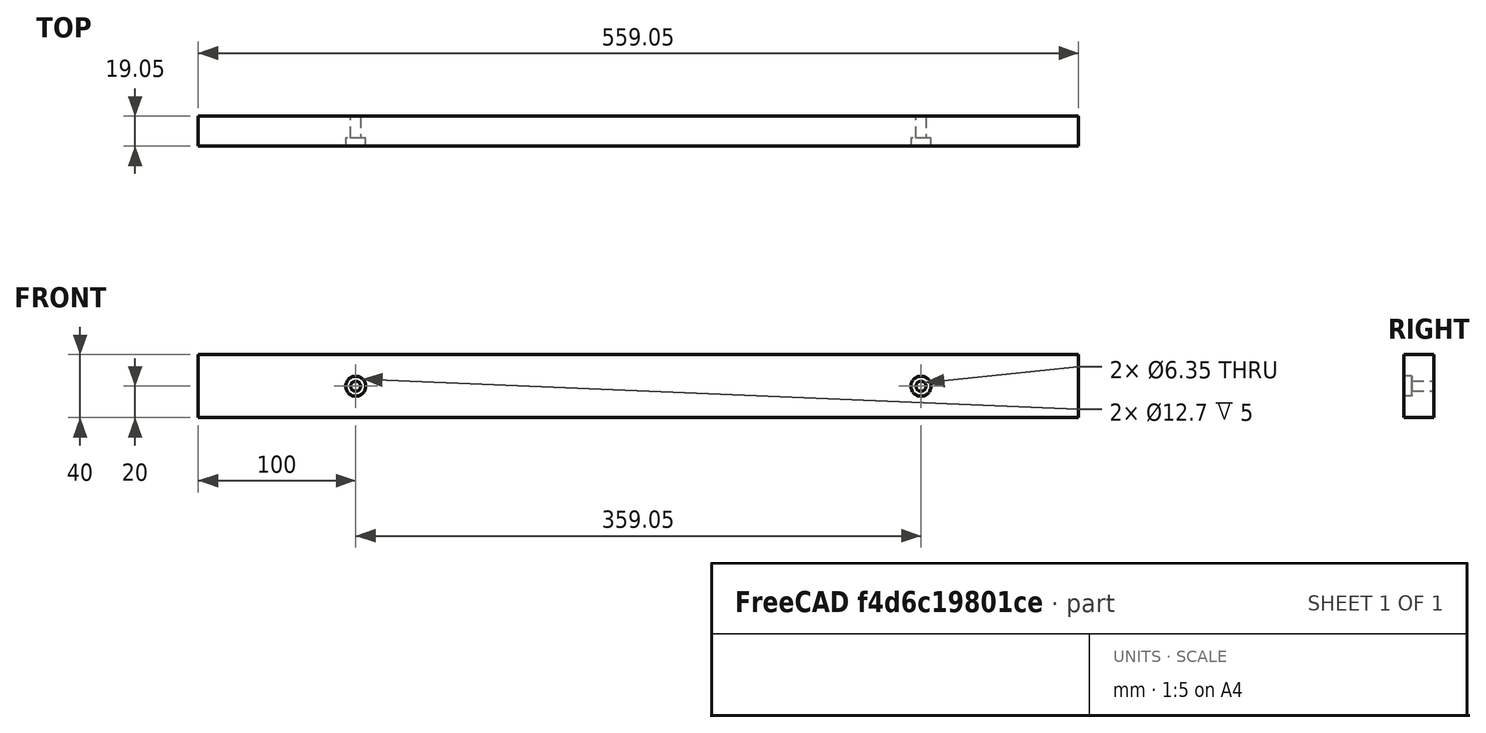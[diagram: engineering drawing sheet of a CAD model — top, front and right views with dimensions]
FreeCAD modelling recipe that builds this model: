
FCSTD DOCUMENT  (FreeCAD 0.19R24291 (Git))
Label: back
License: All rights reserved
LicenseURL: http://en.wikipedia.org/wiki/All_rights_reserved
objects: TechDraw::DrawViewDimension×4, Sketcher::SketchObject×2, PartDesign::Pad×1, PartDesign::Pocket×1, PartDesign::Body×1, TechDraw::DrawSVGTemplate×1, TechDraw::DrawViewPart×1, TechDraw::DrawPage×1
note: 7 computed .brp shape members not serialized (recipe doc carries the construction recipe); baked Part::Feature solids carry a one-line shape summary decoded from their .brp

FEATURE [Sketcher::SketchObject] Sketch
  FullyConstrained = true
  MapMode = 5
  Placement = pos=(0,0,0) rot=(1,0,0;1.5708rad)
  Support = -> [XZ_Plane]
  expr: Constraints[10] = 540 + 3 / 4 * 25.4
  sketch-geometry (8):
    g0: LineSegment StartX=0 StartY=0 StartZ=0 EndX=559.05 EndY=0 EndZ=0
    g1: LineSegment StartX=559.05 StartY=0 StartZ=0 EndX=559.05 EndY=40 EndZ=0
    g2: LineSegment StartX=559.05 StartY=40 StartZ=0 EndX=0 EndY=40 EndZ=0
    g3: LineSegment StartX=0 StartY=40 StartZ=0 EndX=0 EndY=0 EndZ=0
    g4: LineSegment StartX=0 StartY=20 StartZ=0 EndX=559.05 EndY=20 EndZ=0
    g5: Circle CenterX=100 CenterY=20 CenterZ=0 NormalX=0 NormalY=0 NormalZ=1 AngleXU=0 Radius=3.175
    g6: LineSegment StartX=279.525 StartY=3.6e-15 StartZ=0 EndX=279.525 EndY=40 EndZ=0
    g7: Circle CenterX=459.05 CenterY=20 CenterZ=0 NormalX=0 NormalY=0 NormalZ=1 AngleXU=0 Radius=3.175
  constraints (23):
    c: Coincident(g0,g1)
    c: Coincident(g1,g2)
    c: Coincident(g2,g3)
    c: Coincident(g3,g0)
    c: Horizontal(g0)
    c: Horizontal(g2)
    c: Vertical(g1)
    c: Vertical(g3)
    c: Coincident(g0,g-1)
    c: DistanceY(g3,g3) = 40
    c: DistanceX(g0,g0) = 559.05
    c: Horizontal(g4)
    c: Symmetric(g0,g2,g4)
    c: PointOnObject(g5,g4)
    c: DistanceX(g4,g5) = 100
    c: Parallel(g6,g3)
    c: Symmetric(g2,g1,g6)
    c: PointOnObject(g6,g0)
    c: Diameter(g5) = 6.35
    c: PointOnObject(g4,g1)
    c: Diameter(g7) = 6.35
    c: DistanceX(g7,g4) = 100
    c: PointOnObject(g7,g4)
FEATURE [PartDesign::Pad] Pad
  Direction = (1,1,1)
  Length = 19.05
  Length2 = 100
  Placement = pos=(0,0,0) rot=(1,0,0;1.5708rad)
  Profile = -> Sketch
  Type = 0
  expr: Length = 3 / 4 * 25.4
FEATURE [Sketcher::SketchObject] Sketch001
  ExternalGeometry = -> [Pad]
  FullyConstrained = true
  MapMode = 5
  Placement = pos=(0,-19.05,-4.2e-15) rot=(1,0,0;1.5708rad)
  Support = -> [Pad]
  expr: Constraints[1] = 1 / 2 * 25.4
  sketch-geometry (2):
    g0: Circle CenterX=100 CenterY=20 CenterZ=0 NormalX=0 NormalY=0 NormalZ=1 AngleXU=0 Radius=6.35
    g1: Circle CenterX=459.05 CenterY=20 CenterZ=0 NormalX=0 NormalY=0 NormalZ=1 AngleXU=0 Radius=6.35
  constraints (4):
    c: Coincident(g0,g-3)
    c: Diameter(g0) = 12.7
    c: Coincident(g1,g-6)
    c: Equal(g0,g1)
FEATURE [PartDesign::Pocket] Pocket
  BaseFeature = -> Pad
  Length = 5
  Length2 = 100
  Placement = pos=(0,0,0) rot=(1,0,0;1.5708rad)
  Profile = -> Sketch001
  Type = 0
FEATURE [PartDesign::Body] Body
  Group = -> [Sketch,Pad,Sketch001,Pocket]
  Origin = -> Origin
  Tip = -> Pocket
FEATURE [TechDraw::DrawSVGTemplate] Template
  EditableTexts = Designed_by_Name=Designed by Name; Drawing_number=Drawing number; FC-Date=Date; FC-SC=Scale; FC-SH=Sheet; FC-Title=Title; Subtitle=Subtitle; Weight=Weight
  Height = 210
  Orientation = 1
  Width = 297
FEATURE [TechDraw::DrawViewPart] View
  CoarseView = false
  Direction = (0,-1,0)
  Focus = 100
  HardHidden = false
  IsoCount = 0
  IsoHidden = false
  IsoVisible = false
  LockPosition = false
  Perspective = false
  Rotation = 0
  Scale = 0.4
  ScaleType = 0
  SeamHidden = false
  SeamVisible = true
  SmoothHidden = false
  SmoothVisible = true
  Source = -> [Pocket]
  X = 148.5
  XDirection = (1,0,0)
  Y = 105
FEATURE [TechDraw::DrawViewDimension] Dimension
  Arbitrary = false
  ArbitraryTolerances = false
  EqualTolerance = true
  FormatSpec = %.2f
  FormatSpecOverTolerance = %+.2f
  FormatSpecUnderTolerance = %+.2f
  Inverted = false
  LockPosition = false
  MeasureType = 1
  OverTolerance = 0
  References2D = -> [View]
  Rotation = 0
  Scale = 0.4
  ScaleType = 0
  TheoreticalExact = false
  Type = 1
  UnderTolerance = 0
  X = 1.40843
  Y = 36.732
FEATURE [TechDraw::DrawViewDimension] Dimension001
  Arbitrary = false
  ArbitraryTolerances = false
  EqualTolerance = true
  FormatSpec = %.2f
  FormatSpecOverTolerance = %+.2f
  FormatSpecUnderTolerance = %+.2f
  Inverted = false
  LockPosition = false
  MeasureType = 1
  OverTolerance = 0
  References2D = -> [View]
  Rotation = 0
  Scale = 0.4
  ScaleType = 0
  TheoreticalExact = false
  Type = 1
  UnderTolerance = 0
  X = -95.0331
  Y = -21.3828
FEATURE [TechDraw::DrawViewDimension] Dimension002
  Arbitrary = false
  ArbitraryTolerances = false
  EqualTolerance = true
  FormatSpec = %.2f
  FormatSpecOverTolerance = %+.2f
  FormatSpecUnderTolerance = %+.2f
  Inverted = false
  LockPosition = false
  MeasureType = 1
  OverTolerance = 0
  References2D = -> [View]
  Rotation = 0
  Scale = 0.4
  ScaleType = 0
  TheoreticalExact = false
  Type = 2
  UnderTolerance = 0
  X = -119.658
  Y = -19.8485
FEATURE [TechDraw::DrawViewDimension] Dimension003
  Arbitrary = false
  ArbitraryTolerances = false
  EqualTolerance = true
  FormatSpec = %.2f
  FormatSpecOverTolerance = %+.2f
  FormatSpecUnderTolerance = %+.2f
  Inverted = false
  LockPosition = false
  MeasureType = 1
  OverTolerance = 0
  References2D = -> [View]
  Rotation = 0
  Scale = 0.4
  ScaleType = 0
  TheoreticalExact = false
  Type = 2
  UnderTolerance = 0
  X = 114.744
  Y = -27.5817
FEATURE [TechDraw::DrawPage] Page
  KeepUpdated = true
  NextBalloonIndex = 1
  ProjectionType = 0
  Scale = 0.4
  Template = -> Template
  Views = -> [View,Dimension,Dimension001,Dimension002,Dimension003]
